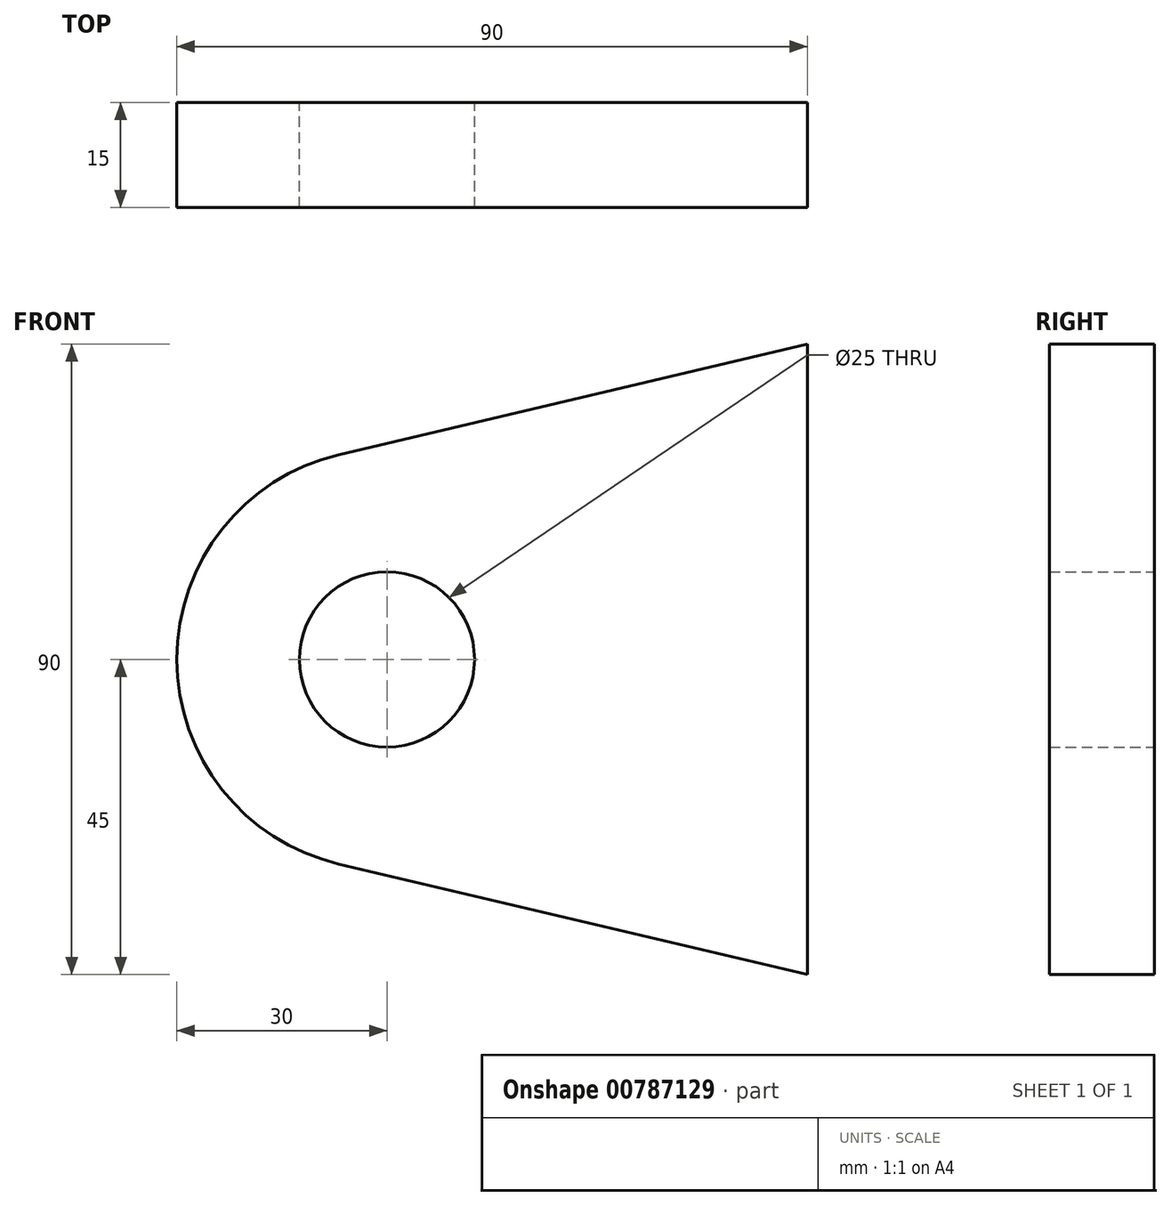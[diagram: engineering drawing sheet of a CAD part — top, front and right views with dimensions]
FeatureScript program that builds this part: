
annotation { "Feature Type Name" : "Feature", "Feature Type Description" : "" }
export const myFeature = defineFeature(function(context is Context, id is Id, definition is map)
    precondition{}
    {
        {
            var Q0;
            Q0=qCreatedBy(makeId("Front.planeOp"),FACE);
            var sketch = newSketch(context, id + "F0", { "sketchPlane" : qUnion([Q0])});
            skCircle(sketch, "E0", {"center": v(-60, 0) * mm, "radius": 12.5 * mm});
            skCircle(sketch, "E1", {"center": v(-60, 0) * mm, "radius": 30 * mm});
            skLineSegment(sketch, "E2", {"start": v(0, 45) * mm, "end": v(-66.9, 29.2) * mm});
            skLineSegment(sketch, "E3.MirrorCS", {"start": v(0, -45) * mm, "end": v(-66.9, -29.2) * mm});
            skLineSegment(sketch, "E4", {"start": v(0, 45) * mm, "end": v(0, -45) * mm});
            skSolve(sketch);
        }
        {
            var Q0;
            Q0=makeQuery(id+"F0.imprint","IMPRINT",FACE,{"disambiguationData":[TD([[makeQuery(id+"F0.imprint","IMPRINT",EDGE,{"derivedFrom":sQuery(id+"F0.wireOp",EDGE,"E0")}),-1.0]])]});
            var Q1;
            {var subQ0=sQuery(id+"F0.wireOp",EDGE,"E2");Q1=makeQuery(id+"F0.imprint","IMPRINT",FACE,{"disambiguationData":[TD([[makeQuery(id+"F0.imprint","IMPRINT",EDGE,{"derivedFrom":subQ0}),1.0]])]});}
            extrude(context, id + "F1", {"entities" : qUnion([Q0, Q1]), "depth" : 15 * mm, "offsetDistance" : 25 * mm});
        }
    });
